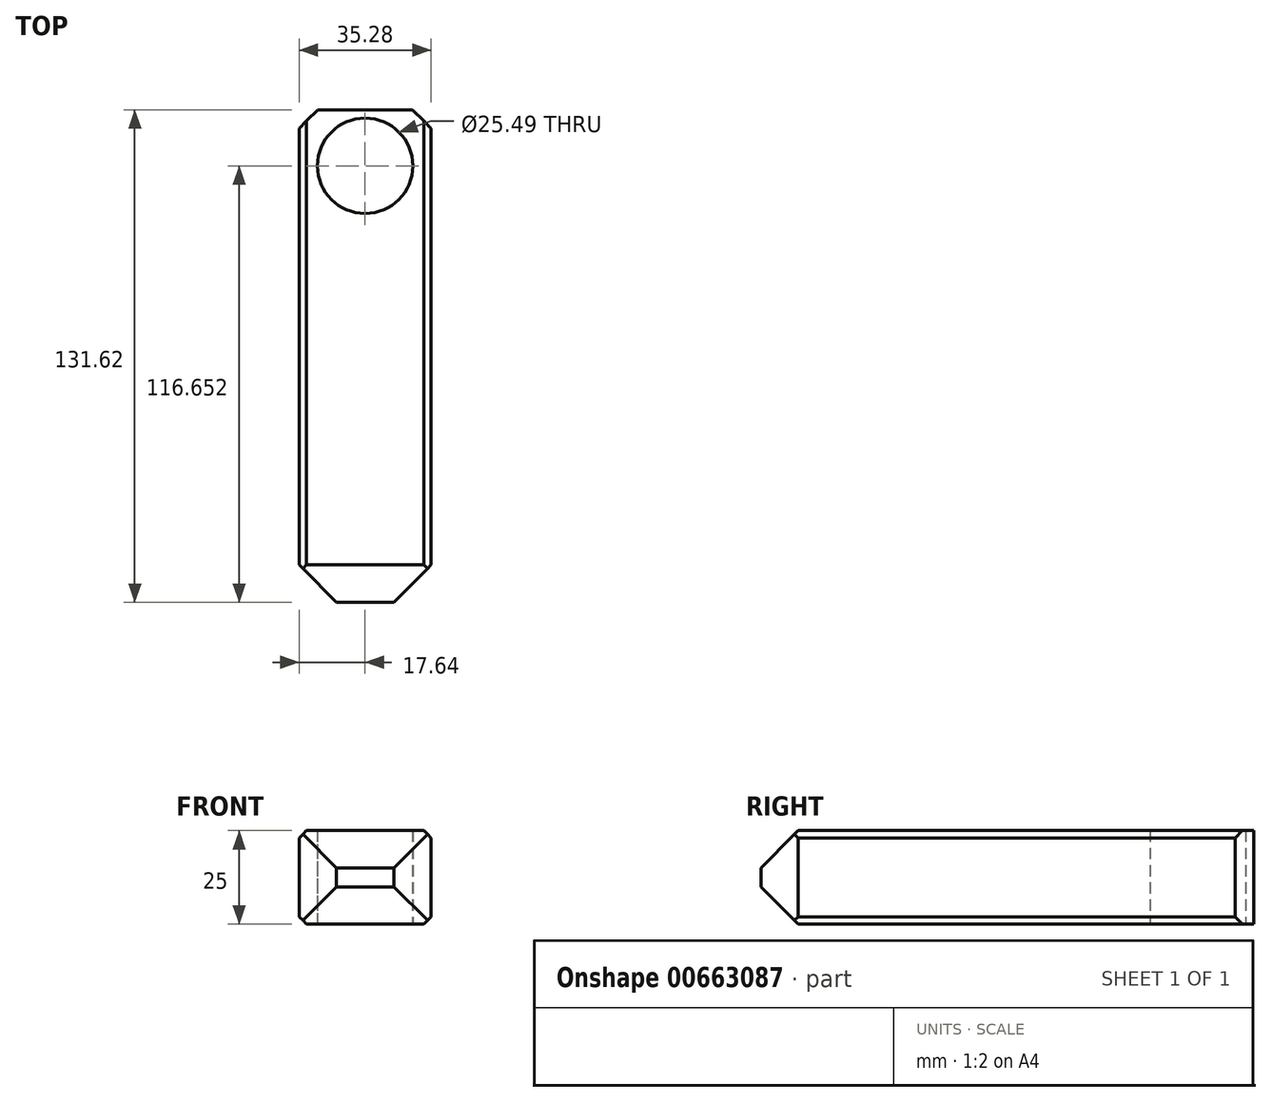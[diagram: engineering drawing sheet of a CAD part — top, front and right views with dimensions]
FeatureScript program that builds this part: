
annotation { "Feature Type Name" : "Feature", "Feature Type Description" : "" }
export const myFeature = defineFeature(function(context is Context, id is Id, definition is map)
    precondition{}
    {
        {
            var Q0;
            Q0=qCreatedBy(makeId("Top.planeOp"),FACE);
            var sketch = newSketch(context, id + "F0", { "sketchPlane" : qUnion([Q0])});
            skLineSegment(sketch, "E0.bottom", {"start": v(17.64, 40.81) * mm, "end": v(-17.64, 40.81) * mm});
            skLineSegment(sketch, "E0.top", {"start": v(17.64, -40.81) * mm, "end": v(-17.64, -40.81) * mm});
            skLineSegment(sketch, "E0.left", {"start": v(17.64, 40.81) * mm, "end": v(17.64, -40.81) * mm});
            skLineSegment(sketch, "E0.right", {"start": v(-17.64, 40.81) * mm, "end": v(-17.64, -40.81) * mm});
            skPoint(sketch, "E0.middle", {"position": v(0, 0) * mm});
            skSolve(sketch);
        }
        {
            var Q0;
            Q0 = qSketchRegion(id + "F0", true);
            extrude(context, id + "F1", {"entities" : qUnion([Q0]), "depth" : 25 * mm, "offsetDistance" : 25 * mm});
        }
        {
            var Q0;
            Q0=qCreatedBy(makeId("Top.planeOp"),FACE);
            var sketch = newSketch(context, id + "F2", { "sketchPlane" : qUnion([Q0])});
            skCircle(sketch, "E1", {"center": v(0, 25.84) * mm, "radius": 12.74 * mm});
            skSolve(sketch);
        }
        {
            var Q0;
            Q0 = qSketchRegion(id + "F2", true);
            extrude(context, id + "F3", {"entities" : qUnion([Q0]), "operationType" : NewBodyOperationType.REMOVE, "depth" : 25 * mm, "offsetDistance" : 25 * mm});
        }
        {
            var Q0;
            Q0=makeQuery(id+"F1.opExtrude","SWEPT_FACE",FACE,{"disambiguationData":[OSD([sQuery(id+"F0.wireOp",EDGE,"E0.top")])]});
            extrude(context, id + "F4", {"entities" : qUnion([Q0]), "operationType" : NewBodyOperationType.ADD, "depth" : 50 * mm, "offsetDistance" : 25 * mm});
        }
        {
            var Q0;
            Q0=makeQuery(id+"F1.opExtrude","SWEPT_EDGE",EDGE,{"disambiguationData":[OSD([sQuery(id+"F0.wireOp",EDGE,"E0.bottom"),sQuery(id+"F0.wireOp",EDGE,"E0.right")])]});
            var Q1;
            Q1=makeQuery(id+"F1.opExtrude","SWEPT_EDGE",EDGE,{"disambiguationData":[OSD([sQuery(id+"F0.wireOp",EDGE,"E0.bottom"),sQuery(id+"F0.wireOp",EDGE,"E0.left")])]});
            chamfer(context, id + "F5", {"entities" : qUnion([Q0, Q1]), "width" : 5 * mm, "tangentPropagation" : true});
        }
        {
            var Q0;
            {var subQ0=sQuery(id+"F0.wireOp",EDGE,"E0.left");var subQ1=sQuery(id+"F0.wireOp",EDGE,"E0.top");Q0=makeQuery(id+"F4.boolean.opBoolean","MERGE",EDGE,{"derivedFrom":[makeQuery(id+"F1.opExtrude","CAP_EDGE",EDGE,{"disambiguationData":[OSD([subQ0])],"isStart":false}),makeQuery(id+"F4.opExtrude","SWEPT_EDGE",EDGE,{"disambiguationData":[OSD([subQ1,subQ0]),TDD([makeQuery(id+"F1.opExtrude","CAP_VERTEX",VERTEX,{"disambiguationData":[OSD([subQ1,subQ0])],"isStart":false})])]})]});}
            var Q1;
            {var subQ0=sQuery(id+"F0.wireOp",EDGE,"E0.right");var subQ1=sQuery(id+"F0.wireOp",EDGE,"E0.top");Q1=makeQuery(id+"F4.boolean.opBoolean","MERGE",EDGE,{"derivedFrom":[makeQuery(id+"F1.opExtrude","CAP_EDGE",EDGE,{"disambiguationData":[OSD([subQ0])],"isStart":false}),makeQuery(id+"F4.opExtrude","SWEPT_EDGE",EDGE,{"disambiguationData":[OSD([subQ1,subQ0]),TDD([makeQuery(id+"F1.opExtrude","CAP_VERTEX",VERTEX,{"disambiguationData":[OSD([subQ1,subQ0])],"isStart":false})])]})]});}
            var Q2;
            {var subQ0=sQuery(id+"F0.wireOp",EDGE,"E0.left");var subQ1=sQuery(id+"F0.wireOp",EDGE,"E0.top");Q2=makeQuery(id+"F4.boolean.opBoolean","MERGE",EDGE,{"derivedFrom":[makeQuery(id+"F1.opExtrude","CAP_EDGE",EDGE,{"disambiguationData":[OSD([subQ0])],"isStart":true}),makeQuery(id+"F4.opExtrude","SWEPT_EDGE",EDGE,{"disambiguationData":[OSD([subQ1,subQ0]),TDD([makeQuery(id+"F1.opExtrude","CAP_VERTEX",VERTEX,{"disambiguationData":[OSD([subQ1,subQ0])],"isStart":true})])]})]});}
            var Q3;
            {var subQ0=sQuery(id+"F0.wireOp",EDGE,"E0.right");var subQ1=sQuery(id+"F0.wireOp",EDGE,"E0.top");Q3=makeQuery(id+"F4.boolean.opBoolean","MERGE",EDGE,{"derivedFrom":[makeQuery(id+"F1.opExtrude","CAP_EDGE",EDGE,{"disambiguationData":[OSD([subQ0])],"isStart":true}),makeQuery(id+"F4.opExtrude","SWEPT_EDGE",EDGE,{"disambiguationData":[OSD([subQ1,subQ0]),TDD([makeQuery(id+"F1.opExtrude","CAP_VERTEX",VERTEX,{"disambiguationData":[OSD([subQ1,subQ0])],"isStart":true})])]})]});}
            chamfer(context, id + "F6", {"entities" : qUnion([Q0, Q1, Q2, Q3]), "width" : 2 * mm, "tangentPropagation" : true});
        }
        {
            var Q0;
            {var subQ0=sQuery(id+"F0.wireOp",EDGE,"E0.top");Q0=makeQuery(id+"F4.opExtrude","CAP_EDGE",EDGE,{"disambiguationData":[OSD([subQ0]),TDD([makeQuery(id+"F1.opExtrude","CAP_EDGE",EDGE,{"disambiguationData":[OSD([subQ0])],"isStart":false})])],"isStart":false});}
            var Q1;
            Q1=makeQuery(id+"F4.opExtrude","CAP_EDGE",EDGE,{"disambiguationData":[OSD([sQuery(id+"F0.wireOp",EDGE,"E0.top"),sQuery(id+"F0.wireOp",EDGE,"E0.left")])],"isStart":false});
            var Q2;
            {var subQ0=sQuery(id+"F0.wireOp",EDGE,"E0.top");Q2=makeQuery(id+"F4.opExtrude","CAP_EDGE",EDGE,{"disambiguationData":[OSD([subQ0]),TDD([makeQuery(id+"F1.opExtrude","CAP_EDGE",EDGE,{"disambiguationData":[OSD([subQ0])],"isStart":true})])],"isStart":false});}
            var Q3;
            Q3=makeQuery(id+"F4.opExtrude","CAP_EDGE",EDGE,{"disambiguationData":[OSD([sQuery(id+"F0.wireOp",EDGE,"E0.top"),sQuery(id+"F0.wireOp",EDGE,"E0.right")])],"isStart":false});
            chamfer(context, id + "F7", {"entities" : qUnion([Q0, Q1, Q2, Q3]), "width" : 10 * mm, "tangentPropagation" : true});
        }
    });
